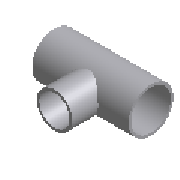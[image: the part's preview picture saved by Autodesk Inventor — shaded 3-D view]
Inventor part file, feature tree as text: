
AUTODESK INVENTOR PART (.ipt)
format: ipt  version: 2023 (Build 270158000, 158)  size: 178,176 bytes
history: native  units: mm (DEFAULTED — no unit token found)
features: other x6, extrude x4, sketch x4
ambient origin geometry x8: Origin, YZ Plane, XZ Plane, XY Plane, X Axis, Y Axis, Z Axis, Center Point
bodies: Solid1 (feature_tree)
feature tree (14):
  extrude  "Extrusion1"  Depth=382.0mm
  extrude  "Extrusion2"  Depth=139.7mm
  extrude  "Extrusion3"  TaperAngle=0.0deg  [1 undecoded]
  extrude  "Extrusion4"  Depth=191.0mm
  other  "Work Axis1"
  other  "Work Point1"
  other  "Work Axis2"
  other  "Work Point2"
  other  "Work Axis3"
  other  "Work Point3"
  sketch  "Sketch1"  dims[d0=273.0mm d1=382.0mm]
  sketch  "Sketch2"  dims[d2=0.0mm d3=139.7mm]
  sketch  "Sketch3"  dims[d4=191.0mm d5=0.0mm]
  sketch  "Sketch4"  dims[d6=253.0mm d7=191.0mm d8=0.0mm d9=127.1mm d10=191.0mm d11=0.0mm]
note: 1 required parameter value undecoded (feature->parameter linkage not recoverable at this tier; creation-order binding heuristic only, values carry confidence <= 0.55)
